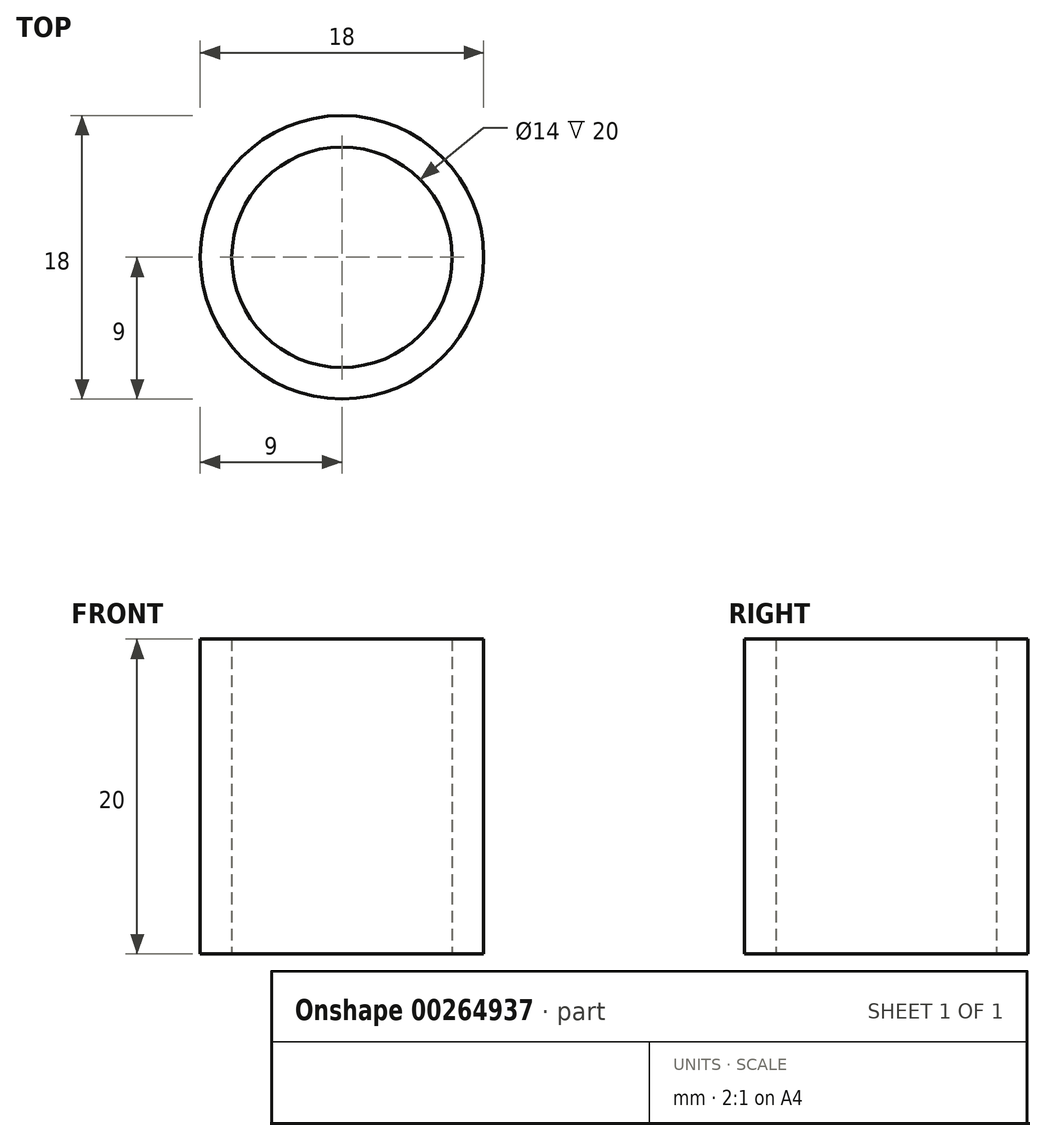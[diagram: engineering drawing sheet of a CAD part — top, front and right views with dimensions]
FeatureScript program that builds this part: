
annotation { "Feature Type Name" : "Feature", "Feature Type Description" : "" }
export const myFeature = defineFeature(function(context is Context, id is Id, definition is map)
    precondition{}
    {
        {
            var Q0;
            Q0=qCreatedBy(makeId("Top.planeOp"),FACE);
            var sketch = newSketch(context, id + "F0", { "sketchPlane" : qUnion([Q0])});
            skCircle(sketch, "E0", {"center": v(0, 0) * mm, "radius": 7 * mm});
            skCircle(sketch, "E1", {"center": v(0, 0) * mm, "radius": 9 * mm});
            skSolve(sketch);
        }
        {
            var Q0;
            Q0 = qSketchRegion(id + "F0", true);
            extrude(context, id + "F1", {"entities" : qUnion([Q0]), "depth" : 20 * mm, "offsetDistance" : 25 * mm});
        }
    });
